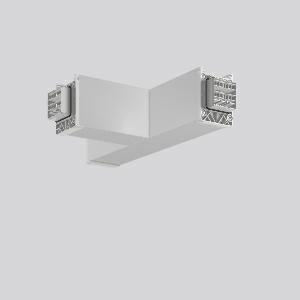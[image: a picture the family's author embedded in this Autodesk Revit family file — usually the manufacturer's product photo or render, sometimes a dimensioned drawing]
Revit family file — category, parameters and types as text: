
# Revit family: linedo_t-verbindung_982774_000_6_d2a2
name_source: partatom
category: Lighting Fixtures
units: mm (PartAtom-declared; Revit-internal decimal feet)

## family parameters
Cut with Voids When Loaded = No
Host = Face
Light Source = No
Part Type = Normal
Room Calculation Point = No
Round Connector Dimension = Use Diameter
Shared = No

## types (1)
- LINEDO T-Verbindung
    Apparent Load = 0 VA
    Default Elevation = 1800 mm
    Description = Series: LINEDO
T-connector, 7-pole, connection plug / socket - plug. Housing: extruded aluminium profile, anodised. Cover made of plastic, surface like housing. LINEDO plug system, plastic, light grey. Easy connection for rigid or flexible wires. 5 membrane cable entries (2 x M20 and 3 x M25). Suitable for power supply in 7-pole version. Ready prewired. Colour-coded individual cables enable easy electromechanical separation.
Colour: anodised aluminium
Length: 330 mm
Width: 204 mm
Height: 76 mm
Weight: 940 g
    Height = 76 mm
    Lamp = 0 x
    Length = 331 mm
    Luminous efficacy = 0 lm/W
    Manufacturer = RZB
    ModVariant = No
    Model = 982774.000.6
    Mounting Place = Ceiling
    Mounting Type = Surface mounted
    Number of Poles = 1
    OnlyDefault = Yes
    Power Factor = 1
    Product Name = LINEDO T-Verbindung
    Product group = Surface mounted continuous line luminaire system
    ProductGroupID = 310
    Protection Class = Protection class I
    Protection Degree = Degree of protection
    RLX_Detail_Level = 1
    RLX_Emergency_Light_Flux = 0 lm
    RLX_Emergency_Type = 0
    RLX_Emergency_Type_DB = No
    RlxData = <blob elided: 18201 chars, md5=ef70f4bc>
    Standby Power = 0 W
    System Light Flux = 0 lm
    System Power = 0 W
    Type Comments = Product without accessories
    Type Image = 982774.000.2.jpg
    URL = http://relux.com
    VarID = ---
    Voltage = 0 V
    Weight = 0.00 kg
    Width = 204 mm

## geometry (parser evidence)
native form markers: Blend x4, Sweep x10
no freeform markers — native parametric forms only
